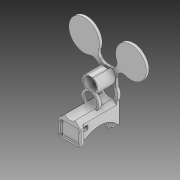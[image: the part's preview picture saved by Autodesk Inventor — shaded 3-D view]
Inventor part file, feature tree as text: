
AUTODESK INVENTOR PART (.ipt)
format: ipt  version: 2020 (Build 240168000, 168)  size: 449,536 bytes
history: native  units: mm
features: extrude x14, sketch x14, fillet x3, chamfer x3, mirror x1
ambient origin geometry x8: Origin, YZ Plane, XZ Plane, XY Plane, X Axis, Y Axis, Z Axis, Center Point
bodies: Solid1 (feature_tree)
feature tree (35):
  extrude  "Extrusion1"  Depth=20.6375mm
  extrude  "Extrusion2"  Depth=3.96875mm
  extrude  "Extrusion3"  Depth=19.05mm
  extrude  "Extrusion4"  Depth=5.5mm
  extrude  "Extrusion5"  Depth=3.0mm
  extrude  "Extrusion7"  Depth=9.0mm
  extrude  "Extrusion8"  TaperAngle=45.0deg  [1 undecoded]
  mirror  "Mirror2"
  fillet  "Fillet2"  Radius=2.0mm
  extrude  "Extrusion9"  Depth=1.0mm
  chamfer  "Chamfer1"  Distance=7.75mm
  extrude  "Extrusion10"  Depth=3.0mm
  extrude  "Extrusion11"  Depth=18.0mm
  extrude  "Extrusion12"  Depth=3.0mm TaperAngle=0.0deg
  fillet  "Fillet3"  Radius=2.5mm
  extrude  "Extrusion13"  Depth=2.0mm TaperAngle=0.0deg
  fillet  "Fillet4"  Radius=2.5mm
  extrude  "Extrusion14"  Depth=10.0mm TaperAngle=0.0deg
  chamfer  "Chamfer2"  Distance=4.2mm
  extrude  "Extrusion15"  Depth=3.0mm TaperAngle=0.0deg
  chamfer  "Chamfer3"  Distance=10.0mm
  sketch  "Sketch1"  dims[d0=20.6375mm d1=23.8125mm d2=32.816122mm]
  sketch  "Sketch2"  dims[d3=23.8125mm d4=3.96875mm]
  sketch  "Sketch3"  dims[d5=19.05mm d6=9.797mm]
  sketch  "Sketch4"  dims[d7=5.5mm d8=16.1mm]
  sketch  "Sketch5"  dims[d9=3.0mm d10=0.0mm d11=14.1mm]
  sketch  "Sketch7"  dims[d12=18.0mm d13=8.0mm d14=9.0mm]
  sketch  "Sketch8"  dims[d15=20.0mm d16=0.0mm d17=45.0deg d18=2.0mm]
  sketch  "Sketch9"  dims[d19=0.0mm d20=0.0mm d21=1.0mm]
  sketch  "Sketch10"  dims[d22=1.0mm]
  sketch  "Sketch11"  dims[d23=2.5mm d24=7.75mm d25=0.0mm]
  sketch  "Sketch12"  dims[d26=9.5mm d27=3.0mm]
  sketch  "Sketch13"  dims[d28=40.0mm d29=0.0mm d33=18.0mm]
  sketch  "Sketch14"  dims[d34=26.0mm d35=3.0mm d36=0.0mm]
  sketch  "Sketch15"  dims[d37=2.4mm d38=12.5mm d39=20.5mm d40=2.5mm d41=2.0mm d42=0.0mm d43=2.5mm d44=10.0mm d45=0.0mm d46=4.2mm d47=7.75mm d48=0.0mm d49=10.0mm d50=0.0mm d51=3.0mm d52=1.5mm d53=0.0mm d54=2.5mm d55=12.0mm d56=2.0mm d57=45.0deg d58=27.0mm d59=35.0mm d60=1.5mm d61=0.0mm d62=7.0mm d63=0.5mm d64=2.0mm d65=45.0deg d66=2.0mm d67=3.0mm d68=0.0mm d69=11.90625mm d70=45.0deg d71=45.0deg d72=26.876241mm d73=6.0mm d74=3.5mm d75=2.5mm d76=2.0mm d77=0.0mm d78=1.0mm d79=3.0mm d80=45.0deg]
note: 1 required parameter value undecoded (feature->parameter linkage not recoverable at this tier; creation-order binding heuristic only, values carry confidence <= 0.55)
